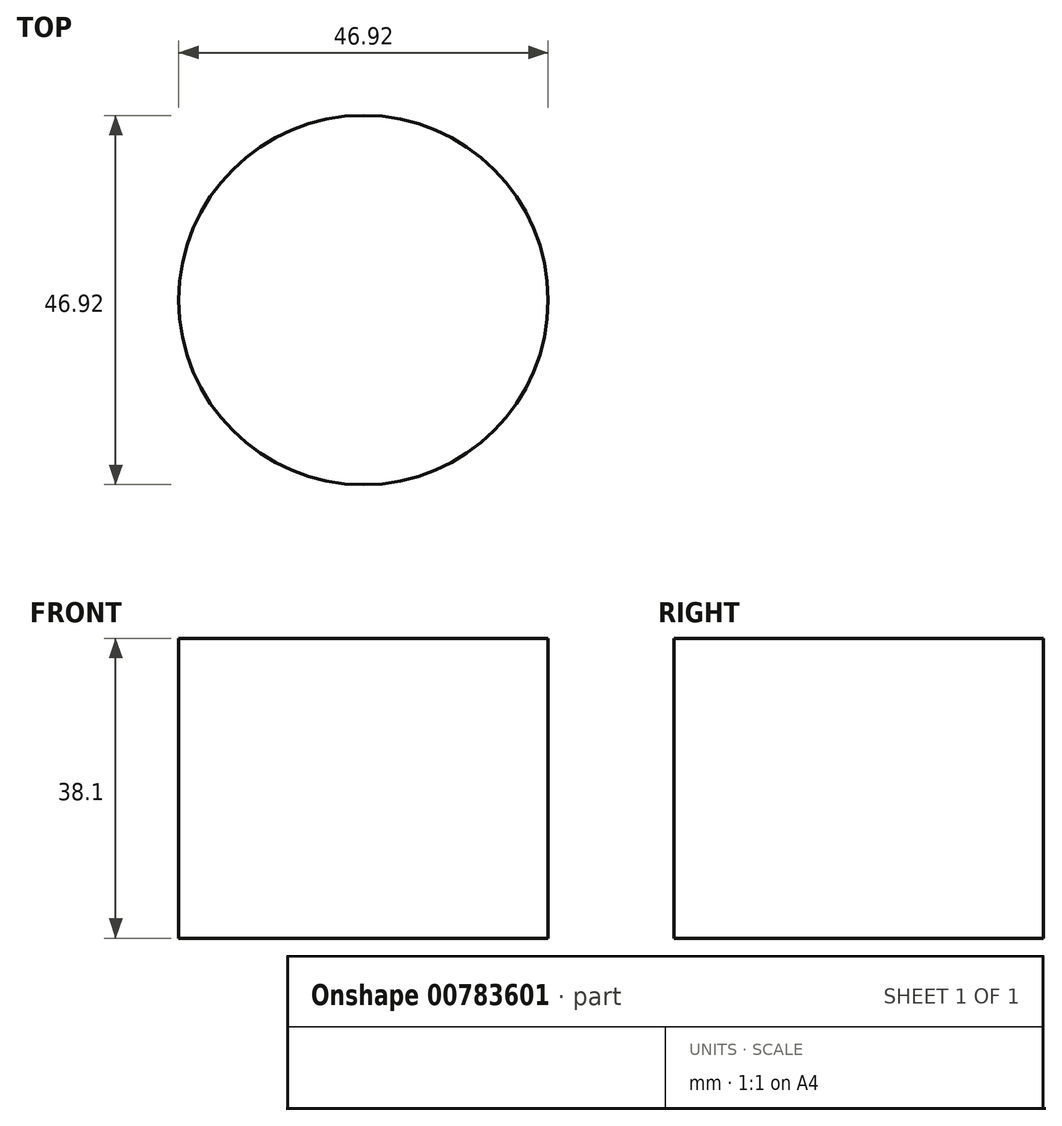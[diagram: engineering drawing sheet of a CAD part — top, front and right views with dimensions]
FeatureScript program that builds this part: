
annotation { "Feature Type Name" : "Feature", "Feature Type Description" : "" }
export const myFeature = defineFeature(function(context is Context, id is Id, definition is map)
    precondition{}
    {
        {
            var Q0;
            Q0=qCreatedBy(makeId("Top.planeOp"),FACE);
            var sketch = newSketch(context, id + "F0", { "sketchPlane" : qUnion([Q0])});
            skCircle(sketch, "E0", {"center": v(12.02, 24.66) * mm, "radius": 23.46 * mm});
            skSolve(sketch);
        }
        {
            var Q0;
            Q0=makeQuery(id+"F0.imprint","IMPRINT",FACE,{"disambiguationData":[TD([[makeQuery(id+"F0.imprint","IMPRINT",EDGE,{"derivedFrom":sQuery(id+"F0.wireOp",EDGE,"E0")}),1.0]])]});
            extrude(context, id + "F1", {"entities" : qUnion([Q0]), "depth" : 80.61 * mm, "offsetDistance" : 25.4 * mm});
        }
        {
            var Q0;
            Q0=makeQuery(id+"F1.opExtrude","SWEPT_FACE",FACE,{"disambiguationData":[OSD([sQuery(id+"F0.wireOp",EDGE,"E0")])]});
            var Q1;
            Q1=makeQuery(id+"F1.opExtrude","CAP_FACE",FACE,{"disambiguationData":[OSD([sQuery(id+"F0.wireOp",EDGE,"E0")])],"isStart":false});
            shell(context, id + "F2", {"entities" : qUnion([Q0, Q1]), "thickness" : 38.1 * mm});
        }
    });
